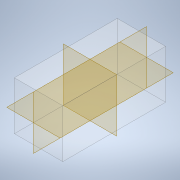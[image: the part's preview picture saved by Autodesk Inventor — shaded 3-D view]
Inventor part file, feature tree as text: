
AUTODESK INVENTOR PART (.ipt)
format: ipt  version: 2020 (Build 240168000, 168)  size: 101,888 bytes
history: native  units: in
note: dims shown in document units (in); Inventor stores cm internally (conversion verified against a paired STEP export)
features: plane x3, extrude x1, sketch x1
ambient origin geometry x8: Origin, YZ Plane, XZ Plane, XY Plane, X Axis, Y Axis, Z Axis, Center Point
bodies: Solid1 (feature_tree)
feature tree (5):
  extrude  "Extrusion1"  Depth=48.0in
  plane  "Work Plane1"
  plane  "Work Plane2"
  plane  "Work Plane3"
  sketch  "Sketch1"  dims[d0=48.0in d1=48.0in d2=102.0in d3=0.0in d4=-24.0in d5=-24.0in d6=-51.0in]
